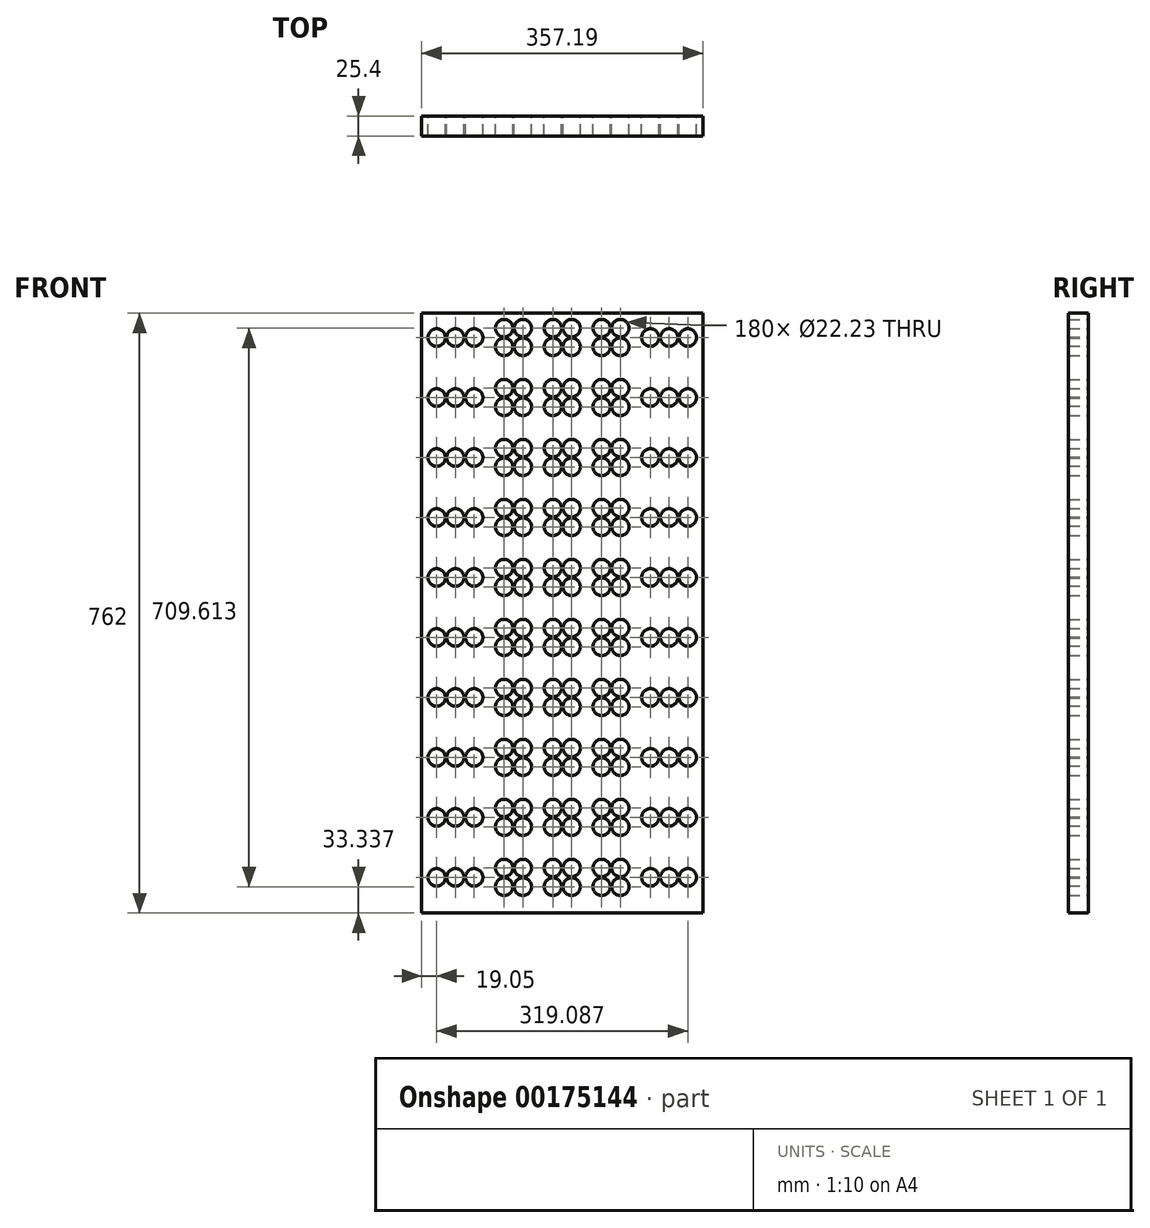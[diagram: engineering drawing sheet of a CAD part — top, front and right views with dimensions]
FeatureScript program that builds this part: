
annotation { "Feature Type Name" : "Feature", "Feature Type Description" : "" }
export const myFeature = defineFeature(function(context is Context, id is Id, definition is map)
    precondition{}
    {
        {
            var Q0;
            Q0=qCreatedBy(makeId("Front.planeOp"),FACE);
            var sketch = newSketch(context, id + "F0", { "sketchPlane" : qUnion([Q0])});
            skLineSegment(sketch, "E0", {"start": v(0, 0) * mm, "end": v(0, 762) * mm});
            skLineSegment(sketch, "E1", {"start": v(0, 762) * mm, "end": v(357.19, 762) * mm});
            skLineSegment(sketch, "E2", {"start": v(357.19, 762) * mm, "end": v(357.19, 0) * mm});
            skLineSegment(sketch, "E3", {"start": v(357.19, 0) * mm, "end": v(0, 0) * mm});
            skCircle(sketch, "E4", {"center": v(137.16, 742.95) * mm, "radius": 11.11 * mm});
            skCircle(sketch, "E5", {"center": v(137.16, 719.14) * mm, "radius": 11.11 * mm});
            skCircle(sketch, "E6", {"center": v(160.97, 742.95) * mm, "radius": 11.11 * mm});
            skCircle(sketch, "E7", {"center": v(160.97, 719.14) * mm, "radius": 11.11 * mm});
            skLineSegment(sketch, "E8", {"start": v(137.16, 742.95) * mm, "end": v(160.97, 742.95) * mm, "construction": true});
            skLineSegment(sketch, "E9", {"start": v(160.97, 719.14) * mm, "end": v(160.97, 742.95) * mm, "construction": true});
            skLineSegment(sketch, "E10", {"start": v(137.16, 742.95) * mm, "end": v(137.16, 719.14) * mm, "construction": true});
            skLineSegment(sketch, "E11", {"start": v(137.16, 719.14) * mm, "end": v(160.97, 719.14) * mm, "construction": true});
            skCircle(sketch, "E12", {"center": v(196.22, 742.95) * mm, "radius": 11.11 * mm});
            skCircle(sketch, "E13", {"center": v(220.03, 742.95) * mm, "radius": 11.11 * mm});
            skCircle(sketch, "E14", {"center": v(220.03, 719.14) * mm, "radius": 11.11 * mm});
            skCircle(sketch, "E15", {"center": v(196.22, 719.14) * mm, "radius": 11.11 * mm});
            skCircle(sketch, "E16", {"center": v(255.27, 742.95) * mm, "radius": 11.11 * mm});
            skCircle(sketch, "E17", {"center": v(279.08, 742.95) * mm, "radius": 11.11 * mm});
            skCircle(sketch, "E18", {"center": v(255.27, 719.14) * mm, "radius": 11.11 * mm});
            skCircle(sketch, "E19", {"center": v(279.08, 719.14) * mm, "radius": 11.11 * mm});
            skCircle(sketch, "E20", {"center": v(314.33, 742.95) * mm, "radius": 11.11 * mm});
            skCircle(sketch, "E21", {"center": v(314.33, 719.14) * mm, "radius": 11.11 * mm});
            skCircle(sketch, "E22", {"center": v(338.14, 719.14) * mm, "radius": 11.11 * mm});
            skCircle(sketch, "E23", {"center": v(338.14, 742.95) * mm, "radius": 11.11 * mm});
            skLineSegment(sketch, "E24", {"start": v(196.22, 742.95) * mm, "end": v(220.03, 742.95) * mm, "construction": true});
            skLineSegment(sketch, "E25", {"start": v(220.03, 742.95) * mm, "end": v(220.03, 719.14) * mm, "construction": true});
            skLineSegment(sketch, "E26", {"start": v(220.03, 719.14) * mm, "end": v(196.22, 719.14) * mm, "construction": true});
            skLineSegment(sketch, "E27", {"start": v(196.22, 719.14) * mm, "end": v(196.22, 742.95) * mm, "construction": true});
            skLineSegment(sketch, "E28", {"start": v(255.27, 742.95) * mm, "end": v(279.08, 742.95) * mm, "construction": true});
            skLineSegment(sketch, "E29", {"start": v(279.08, 742.95) * mm, "end": v(279.08, 719.14) * mm, "construction": true});
            skLineSegment(sketch, "E30", {"start": v(279.08, 719.14) * mm, "end": v(255.27, 719.14) * mm, "construction": true});
            skLineSegment(sketch, "E31", {"start": v(255.27, 719.14) * mm, "end": v(255.27, 742.95) * mm, "construction": true});
            skLineSegment(sketch, "E32", {"start": v(314.33, 742.95) * mm, "end": v(338.14, 742.95) * mm, "construction": true});
            skLineSegment(sketch, "E33", {"start": v(338.14, 719.14) * mm, "end": v(314.33, 719.14) * mm, "construction": true});
            skLineSegment(sketch, "E34", {"start": v(314.33, 719.14) * mm, "end": v(314.33, 742.95) * mm, "construction": true});
            skLineSegment(sketch, "E35", {"start": v(338.14, 742.95) * mm, "end": v(338.14, 719.14) * mm, "construction": true});
            skLineSegment(sketch, "E36", {"start": v(220.03, 731.04) * mm, "end": v(255.27, 731.04) * mm, "construction": true});
            skLineSegment(sketch, "E37", {"start": v(279.08, 731.04) * mm, "end": v(314.33, 731.04) * mm, "construction": true});
            skLineSegment(sketch, "E38", {"start": v(196.22, 731.04) * mm, "end": v(160.97, 731.04) * mm, "construction": true});
            skCircle(sketch, "E39", {"center": v(19.05, 719.14) * mm, "radius": 11.11 * mm});
            skCircle(sketch, "E40", {"center": v(42.86, 742.95) * mm, "radius": 11.11 * mm});
            skCircle(sketch, "E41", {"center": v(42.86, 719.14) * mm, "radius": 11.11 * mm});
            skCircle(sketch, "E42", {"center": v(19.05, 742.95) * mm, "radius": 11.11 * mm});
            skCircle(sketch, "E43", {"center": v(78.1, 742.95) * mm, "radius": 11.11 * mm});
            skCircle(sketch, "E44", {"center": v(101.92, 742.95) * mm, "radius": 11.11 * mm});
            skCircle(sketch, "E45", {"center": v(101.92, 719.14) * mm, "radius": 11.11 * mm});
            skCircle(sketch, "E46", {"center": v(78.1, 719.14) * mm, "radius": 11.11 * mm});
            skLineSegment(sketch, "E47", {"start": v(19.05, 742.95) * mm, "end": v(42.86, 742.95) * mm, "construction": true});
            skLineSegment(sketch, "E48", {"start": v(42.86, 742.95) * mm, "end": v(42.86, 719.14) * mm, "construction": true});
            skLineSegment(sketch, "E49", {"start": v(19.05, 719.14) * mm, "end": v(42.86, 719.14) * mm, "construction": true});
            skLineSegment(sketch, "E50", {"start": v(19.05, 719.14) * mm, "end": v(19.05, 742.95) * mm, "construction": true});
            skLineSegment(sketch, "E51", {"start": v(78.1, 742.95) * mm, "end": v(101.92, 742.95) * mm, "construction": true});
            skLineSegment(sketch, "E52", {"start": v(101.92, 742.95) * mm, "end": v(101.92, 719.14) * mm, "construction": true});
            skLineSegment(sketch, "E53", {"start": v(101.92, 719.14) * mm, "end": v(78.1, 719.14) * mm, "construction": true});
            skLineSegment(sketch, "E54", {"start": v(78.1, 719.14) * mm, "end": v(78.1, 742.95) * mm, "construction": true});
            skLineSegment(sketch, "E55", {"start": v(42.86, 731.04) * mm, "end": v(78.1, 731.04) * mm, "construction": true});
            skLineSegment(sketch, "E56", {"start": v(19.05, 731.04) * mm, "end": v(0, 731.04) * mm, "construction": true});
            skLineSegment(sketch, "E57", {"start": v(338.14, 731.04) * mm, "end": v(357.19, 731.04) * mm, "construction": true});
            skLineSegment(sketch, "E58", {"start": v(101.92, 731.04) * mm, "end": v(137.16, 731.04) * mm, "construction": true});
            skLineSegment(sketch, "E59", {"start": v(326.23, 742.95) * mm, "end": v(326.23, 762) * mm, "construction": true});
            skLineSegment(sketch, "E60", {"start": v(113.03, 742.95) * mm, "end": v(113.03, 719.14) * mm, "construction": true});
            skLineSegment(sketch, "E61", {"start": v(126.05, 742.95) * mm, "end": v(126.05, 719.14) * mm, "construction": true});
            skSolve(sketch);
        }
        {
            var Q0;
            Q0=qCreatedBy(makeId("Front.planeOp"),FACE);
            var sketch = newSketch(context, id + "F1", { "sketchPlane" : qUnion([Q0])});
            skLineSegment(sketch, "E62", {"start": v(0, 0) * mm, "end": v(0, 762) * mm});
            skLineSegment(sketch, "E63", {"start": v(0, 762) * mm, "end": v(357.19, 762) * mm});
            skLineSegment(sketch, "E64", {"start": v(357.19, 762) * mm, "end": v(357.19, 0) * mm});
            skLineSegment(sketch, "E65", {"start": v(357.19, 0) * mm, "end": v(0, 0) * mm});
            skCircle(sketch, "E66", {"center": v(166.69, 742.95) * mm, "radius": 11.11 * mm});
            skCircle(sketch, "E67", {"center": v(166.69, 719.14) * mm, "radius": 11.11 * mm});
            skCircle(sketch, "E68", {"center": v(190.5, 742.95) * mm, "radius": 11.11 * mm});
            skCircle(sketch, "E69", {"center": v(190.5, 719.14) * mm, "radius": 11.11 * mm});
            skLineSegment(sketch, "E70", {"start": v(166.69, 742.95) * mm, "end": v(190.5, 742.95) * mm, "construction": true});
            skLineSegment(sketch, "E71", {"start": v(190.5, 719.14) * mm, "end": v(190.5, 742.95) * mm, "construction": true});
            skLineSegment(sketch, "E72", {"start": v(166.69, 742.95) * mm, "end": v(166.69, 719.14) * mm, "construction": true});
            skLineSegment(sketch, "E73", {"start": v(166.69, 719.14) * mm, "end": v(190.5, 719.14) * mm, "construction": true});
            skCircle(sketch, "E74", {"center": v(252.41, 742.95) * mm, "radius": 11.11 * mm});
            skCircle(sketch, "E75", {"center": v(228.6, 742.95) * mm, "radius": 11.11 * mm});
            skCircle(sketch, "E76", {"center": v(252.41, 719.14) * mm, "radius": 11.11 * mm});
            skCircle(sketch, "E77", {"center": v(228.6, 719.14) * mm, "radius": 11.11 * mm});
            skCircle(sketch, "E78", {"center": v(314.33, 731.04) * mm, "radius": 11.11 * mm});
            skCircle(sketch, "E79", {"center": v(338.14, 731.04) * mm, "radius": 11.11 * mm});
            skLineSegment(sketch, "E80", {"start": v(228.6, 742.95) * mm, "end": v(252.41, 742.95) * mm, "construction": true});
            skLineSegment(sketch, "E81", {"start": v(228.6, 742.95) * mm, "end": v(228.6, 719.14) * mm, "construction": true});
            skLineSegment(sketch, "E82", {"start": v(252.41, 719.14) * mm, "end": v(228.6, 719.14) * mm, "construction": true});
            skLineSegment(sketch, "E83", {"start": v(252.41, 719.14) * mm, "end": v(252.41, 742.95) * mm, "construction": true});
            skLineSegment(sketch, "E84", {"start": v(338.14, 731.04) * mm, "end": v(314.33, 731.04) * mm, "construction": true});
            skCircle(sketch, "E85", {"center": v(104.78, 719.14) * mm, "radius": 11.11 * mm});
            skCircle(sketch, "E86", {"center": v(128.59, 719.14) * mm, "radius": 11.11 * mm});
            skCircle(sketch, "E87", {"center": v(128.59, 742.95) * mm, "radius": 11.11 * mm});
            skCircle(sketch, "E88", {"center": v(104.78, 742.95) * mm, "radius": 11.11 * mm});
            skLineSegment(sketch, "E89", {"start": v(104.78, 719.14) * mm, "end": v(128.59, 719.14) * mm, "construction": true});
            skLineSegment(sketch, "E90", {"start": v(128.59, 742.95) * mm, "end": v(128.59, 719.14) * mm, "construction": true});
            skLineSegment(sketch, "E91", {"start": v(128.59, 742.95) * mm, "end": v(104.78, 742.95) * mm, "construction": true});
            skLineSegment(sketch, "E92", {"start": v(104.78, 719.14) * mm, "end": v(104.78, 742.95) * mm, "construction": true});
            skLineSegment(sketch, "E93", {"start": v(19.05, 731.04) * mm, "end": v(0, 731.04) * mm, "construction": true});
            skLineSegment(sketch, "E94", {"start": v(338.14, 731.04) * mm, "end": v(357.19, 731.04) * mm, "construction": true});
            skLineSegment(sketch, "E95", {"start": v(139.7, 742.95) * mm, "end": v(139.7, 719.14) * mm, "construction": true});
            skLineSegment(sketch, "E96", {"start": v(155.57, 742.95) * mm, "end": v(155.57, 719.14) * mm, "construction": true});
            skCircle(sketch, "E97", {"center": v(290.51, 731.04) * mm, "radius": 11.11 * mm});
            skCircle(sketch, "E98", {"center": v(19.05, 731.04) * mm, "radius": 11.11 * mm});
            skCircle(sketch, "E99", {"center": v(42.86, 731.04) * mm, "radius": 11.11 * mm});
            skCircle(sketch, "E100", {"center": v(66.68, 731.04) * mm, "radius": 11.11 * mm});
            skLineSegment(sketch, "E101", {"start": v(19.05, 731.04) * mm, "end": v(42.86, 731.04) * mm, "construction": true});
            skLineSegment(sketch, "E102", {"start": v(42.86, 731.04) * mm, "end": v(66.68, 731.04) * mm, "construction": true});
            skLineSegment(sketch, "E103", {"start": v(290.51, 731.04) * mm, "end": v(314.33, 731.04) * mm, "construction": true});
            skLineSegment(sketch, "E104", {"start": v(252.41, 731.04) * mm, "end": v(290.51, 731.04) * mm, "construction": true});
            skLineSegment(sketch, "E105", {"start": v(228.6, 731.04) * mm, "end": v(190.5, 731.04) * mm, "construction": true});
            skLineSegment(sketch, "E106", {"start": v(128.59, 731.04) * mm, "end": v(166.69, 731.04) * mm, "construction": true});
            skLineSegment(sketch, "E107", {"start": v(104.78, 731.04) * mm, "end": v(66.68, 731.04) * mm, "construction": true});
            skLineSegment(sketch, "E108", {"start": v(240.5, 742.95) * mm, "end": v(240.5, 762) * mm, "construction": true});
            skCircle(sketch, "E109.0.1.0", {"center": v(66.67, 654.84) * mm, "radius": 11.11 * mm});
            skLineSegment(sketch, "E109.0.1.1", {"start": v(19.05, 654.84) * mm, "end": v(42.86, 654.84) * mm, "construction": true});
            skCircle(sketch, "E109.0.1.2", {"center": v(252.41, 642.94) * mm, "radius": 11.11 * mm});
            skLineSegment(sketch, "E109.0.1.3", {"start": v(104.78, 642.94) * mm, "end": v(128.59, 642.94) * mm, "construction": true});
            skLineSegment(sketch, "E109.0.1.4", {"start": v(19.05, 654.84) * mm, "end": v(0, 654.84) * mm, "construction": true});
            skCircle(sketch, "E109.0.1.5", {"center": v(228.6, 642.94) * mm, "radius": 11.11 * mm});
            skLineSegment(sketch, "E109.0.1.6", {"start": v(252.41, 642.94) * mm, "end": v(228.6, 642.94) * mm, "construction": true});
            skCircle(sketch, "E109.0.1.7", {"center": v(19.05, 654.84) * mm, "radius": 11.11 * mm});
            skCircle(sketch, "E109.0.1.8", {"center": v(128.59, 642.94) * mm, "radius": 11.11 * mm});
            skCircle(sketch, "E109.0.1.9", {"center": v(314.33, 654.84) * mm, "radius": 11.11 * mm});
            skCircle(sketch, "E109.0.1.10", {"center": v(338.14, 654.84) * mm, "radius": 11.11 * mm});
            skCircle(sketch, "E109.0.1.11", {"center": v(166.69, 642.94) * mm, "radius": 11.11 * mm});
            skCircle(sketch, "E109.0.1.12", {"center": v(190.5, 642.94) * mm, "radius": 11.11 * mm});
            skCircle(sketch, "E109.0.1.13", {"center": v(104.78, 642.94) * mm, "radius": 11.11 * mm});
            skCircle(sketch, "E109.0.1.14", {"center": v(42.86, 654.84) * mm, "radius": 11.11 * mm});
            skCircle(sketch, "E109.0.1.15", {"center": v(290.51, 654.84) * mm, "radius": 11.11 * mm});
            skLineSegment(sketch, "E109.0.1.16", {"start": v(290.51, 654.84) * mm, "end": v(314.33, 654.84) * mm, "construction": true});
            skCircle(sketch, "E109.0.1.17", {"center": v(128.59, 666.75) * mm, "radius": 11.11 * mm});
            skLineSegment(sketch, "E109.0.1.18", {"start": v(338.14, 654.84) * mm, "end": v(314.33, 654.84) * mm, "construction": true});
            skLineSegment(sketch, "E109.0.1.19", {"start": v(42.86, 654.84) * mm, "end": v(66.67, 654.84) * mm, "construction": true});
            skLineSegment(sketch, "E109.0.1.20", {"start": v(128.59, 666.75) * mm, "end": v(104.78, 666.75) * mm, "construction": true});
            skLineSegment(sketch, "E109.0.1.21", {"start": v(228.6, 654.84) * mm, "end": v(190.5, 654.84) * mm, "construction": true});
            skLineSegment(sketch, "E109.0.1.22", {"start": v(338.14, 654.84) * mm, "end": v(357.19, 654.84) * mm, "construction": true});
            skCircle(sketch, "E109.0.1.23", {"center": v(228.6, 666.75) * mm, "radius": 11.11 * mm});
            skCircle(sketch, "E109.0.1.24", {"center": v(104.78, 666.75) * mm, "radius": 11.11 * mm});
            skLineSegment(sketch, "E109.0.1.25", {"start": v(104.78, 654.84) * mm, "end": v(66.67, 654.84) * mm, "construction": true});
            skCircle(sketch, "E109.0.1.26", {"center": v(166.69, 666.75) * mm, "radius": 11.11 * mm});
            skCircle(sketch, "E109.0.1.27", {"center": v(252.41, 666.75) * mm, "radius": 11.11 * mm});
            skLineSegment(sketch, "E109.0.1.28", {"start": v(166.69, 666.75) * mm, "end": v(190.5, 666.75) * mm, "construction": true});
            skLineSegment(sketch, "E109.0.1.29", {"start": v(166.69, 642.94) * mm, "end": v(190.5, 642.94) * mm, "construction": true});
            skCircle(sketch, "E109.0.1.30", {"center": v(190.5, 666.75) * mm, "radius": 11.11 * mm});
            skLineSegment(sketch, "E109.0.1.31", {"start": v(252.41, 654.84) * mm, "end": v(290.51, 654.84) * mm, "construction": true});
            skLineSegment(sketch, "E109.0.1.32", {"start": v(252.41, 642.94) * mm, "end": v(252.41, 666.75) * mm, "construction": true});
            skLineSegment(sketch, "E109.0.1.33", {"start": v(104.78, 642.94) * mm, "end": v(104.78, 666.75) * mm, "construction": true});
            skLineSegment(sketch, "E109.0.1.34", {"start": v(155.58, 666.75) * mm, "end": v(155.58, 642.94) * mm, "construction": true});
            skLineSegment(sketch, "E109.0.1.35", {"start": v(228.6, 666.75) * mm, "end": v(252.41, 666.75) * mm, "construction": true});
            skLineSegment(sketch, "E109.0.1.36", {"start": v(139.7, 666.75) * mm, "end": v(139.7, 642.94) * mm, "construction": true});
            skLineSegment(sketch, "E109.0.1.37", {"start": v(128.59, 654.84) * mm, "end": v(166.69, 654.84) * mm, "construction": true});
            skLineSegment(sketch, "E109.0.1.38", {"start": v(228.6, 666.75) * mm, "end": v(228.6, 642.94) * mm, "construction": true});
            skLineSegment(sketch, "E109.0.1.39", {"start": v(166.69, 666.75) * mm, "end": v(166.69, 642.94) * mm, "construction": true});
            skLineSegment(sketch, "E109.0.1.40", {"start": v(190.5, 642.94) * mm, "end": v(190.5, 666.75) * mm, "construction": true});
            skLineSegment(sketch, "E109.0.1.41", {"start": v(128.59, 666.75) * mm, "end": v(128.59, 642.94) * mm, "construction": true});
            skCircle(sketch, "E109.0.2.0", {"center": v(66.67, 578.64) * mm, "radius": 11.11 * mm});
            skLineSegment(sketch, "E109.0.2.1", {"start": v(19.05, 578.64) * mm, "end": v(42.86, 578.64) * mm, "construction": true});
            skCircle(sketch, "E109.0.2.2", {"center": v(252.41, 566.74) * mm, "radius": 11.11 * mm});
            skLineSegment(sketch, "E109.0.2.3", {"start": v(104.78, 566.74) * mm, "end": v(128.59, 566.74) * mm, "construction": true});
            skLineSegment(sketch, "E109.0.2.4", {"start": v(19.05, 578.64) * mm, "end": v(0, 578.64) * mm, "construction": true});
            skCircle(sketch, "E109.0.2.5", {"center": v(228.6, 566.74) * mm, "radius": 11.11 * mm});
            skLineSegment(sketch, "E109.0.2.6", {"start": v(252.41, 566.74) * mm, "end": v(228.6, 566.74) * mm, "construction": true});
            skCircle(sketch, "E109.0.2.7", {"center": v(19.05, 578.64) * mm, "radius": 11.11 * mm});
            skCircle(sketch, "E109.0.2.8", {"center": v(128.59, 566.74) * mm, "radius": 11.11 * mm});
            skCircle(sketch, "E109.0.2.9", {"center": v(314.33, 578.64) * mm, "radius": 11.11 * mm});
            skCircle(sketch, "E109.0.2.10", {"center": v(338.14, 578.64) * mm, "radius": 11.11 * mm});
            skCircle(sketch, "E109.0.2.11", {"center": v(166.69, 566.74) * mm, "radius": 11.11 * mm});
            skCircle(sketch, "E109.0.2.12", {"center": v(190.5, 566.74) * mm, "radius": 11.11 * mm});
            skCircle(sketch, "E109.0.2.13", {"center": v(104.78, 566.74) * mm, "radius": 11.11 * mm});
            skCircle(sketch, "E109.0.2.14", {"center": v(42.86, 578.64) * mm, "radius": 11.11 * mm});
            skCircle(sketch, "E109.0.2.15", {"center": v(290.51, 578.64) * mm, "radius": 11.11 * mm});
            skLineSegment(sketch, "E109.0.2.16", {"start": v(290.51, 578.64) * mm, "end": v(314.33, 578.64) * mm, "construction": true});
            skCircle(sketch, "E109.0.2.17", {"center": v(128.59, 590.55) * mm, "radius": 11.11 * mm});
            skLineSegment(sketch, "E109.0.2.18", {"start": v(338.14, 578.64) * mm, "end": v(314.33, 578.64) * mm, "construction": true});
            skLineSegment(sketch, "E109.0.2.19", {"start": v(42.86, 578.64) * mm, "end": v(66.67, 578.64) * mm, "construction": true});
            skLineSegment(sketch, "E109.0.2.20", {"start": v(128.59, 590.55) * mm, "end": v(104.78, 590.55) * mm, "construction": true});
            skLineSegment(sketch, "E109.0.2.21", {"start": v(228.6, 578.64) * mm, "end": v(190.5, 578.64) * mm, "construction": true});
            skLineSegment(sketch, "E109.0.2.22", {"start": v(338.14, 578.64) * mm, "end": v(357.19, 578.64) * mm, "construction": true});
            skCircle(sketch, "E109.0.2.23", {"center": v(228.6, 590.55) * mm, "radius": 11.11 * mm});
            skCircle(sketch, "E109.0.2.24", {"center": v(104.78, 590.55) * mm, "radius": 11.11 * mm});
            skLineSegment(sketch, "E109.0.2.25", {"start": v(104.78, 578.64) * mm, "end": v(66.67, 578.64) * mm, "construction": true});
            skCircle(sketch, "E109.0.2.26", {"center": v(166.69, 590.55) * mm, "radius": 11.11 * mm});
            skCircle(sketch, "E109.0.2.27", {"center": v(252.41, 590.55) * mm, "radius": 11.11 * mm});
            skLineSegment(sketch, "E109.0.2.28", {"start": v(166.69, 590.55) * mm, "end": v(190.5, 590.55) * mm, "construction": true});
            skLineSegment(sketch, "E109.0.2.29", {"start": v(166.69, 566.74) * mm, "end": v(190.5, 566.74) * mm, "construction": true});
            skCircle(sketch, "E109.0.2.30", {"center": v(190.5, 590.55) * mm, "radius": 11.11 * mm});
            skLineSegment(sketch, "E109.0.2.31", {"start": v(252.41, 578.64) * mm, "end": v(290.51, 578.64) * mm, "construction": true});
            skLineSegment(sketch, "E109.0.2.32", {"start": v(252.41, 566.74) * mm, "end": v(252.41, 590.55) * mm, "construction": true});
            skLineSegment(sketch, "E109.0.2.33", {"start": v(104.78, 566.74) * mm, "end": v(104.78, 590.55) * mm, "construction": true});
            skLineSegment(sketch, "E109.0.2.34", {"start": v(155.58, 590.55) * mm, "end": v(155.58, 566.74) * mm, "construction": true});
            skLineSegment(sketch, "E109.0.2.35", {"start": v(228.6, 590.55) * mm, "end": v(252.41, 590.55) * mm, "construction": true});
            skLineSegment(sketch, "E109.0.2.36", {"start": v(139.7, 590.55) * mm, "end": v(139.7, 566.74) * mm, "construction": true});
            skLineSegment(sketch, "E109.0.2.37", {"start": v(128.59, 578.64) * mm, "end": v(166.69, 578.64) * mm, "construction": true});
            skLineSegment(sketch, "E109.0.2.38", {"start": v(228.6, 590.55) * mm, "end": v(228.6, 566.74) * mm, "construction": true});
            skLineSegment(sketch, "E109.0.2.39", {"start": v(166.69, 590.55) * mm, "end": v(166.69, 566.74) * mm, "construction": true});
            skLineSegment(sketch, "E109.0.2.40", {"start": v(190.5, 566.74) * mm, "end": v(190.5, 590.55) * mm, "construction": true});
            skLineSegment(sketch, "E109.0.2.41", {"start": v(128.59, 590.55) * mm, "end": v(128.59, 566.74) * mm, "construction": true});
            skCircle(sketch, "E109.0.3.0", {"center": v(66.67, 502.44) * mm, "radius": 11.11 * mm});
            skLineSegment(sketch, "E109.0.3.1", {"start": v(19.05, 502.44) * mm, "end": v(42.86, 502.44) * mm, "construction": true});
            skCircle(sketch, "E109.0.3.2", {"center": v(252.41, 490.54) * mm, "radius": 11.11 * mm});
            skLineSegment(sketch, "E109.0.3.3", {"start": v(104.78, 490.54) * mm, "end": v(128.59, 490.54) * mm, "construction": true});
            skLineSegment(sketch, "E109.0.3.4", {"start": v(19.05, 502.44) * mm, "end": v(0, 502.44) * mm, "construction": true});
            skCircle(sketch, "E109.0.3.5", {"center": v(228.6, 490.54) * mm, "radius": 11.11 * mm});
            skLineSegment(sketch, "E109.0.3.6", {"start": v(252.41, 490.54) * mm, "end": v(228.6, 490.54) * mm, "construction": true});
            skCircle(sketch, "E109.0.3.7", {"center": v(19.05, 502.44) * mm, "radius": 11.11 * mm});
            skCircle(sketch, "E109.0.3.8", {"center": v(128.59, 490.54) * mm, "radius": 11.11 * mm});
            skCircle(sketch, "E109.0.3.9", {"center": v(314.33, 502.44) * mm, "radius": 11.11 * mm});
            skCircle(sketch, "E109.0.3.10", {"center": v(338.14, 502.44) * mm, "radius": 11.11 * mm});
            skCircle(sketch, "E109.0.3.11", {"center": v(166.69, 490.54) * mm, "radius": 11.11 * mm});
            skCircle(sketch, "E109.0.3.12", {"center": v(190.5, 490.54) * mm, "radius": 11.11 * mm});
            skCircle(sketch, "E109.0.3.13", {"center": v(104.78, 490.54) * mm, "radius": 11.11 * mm});
            skCircle(sketch, "E109.0.3.14", {"center": v(42.86, 502.44) * mm, "radius": 11.11 * mm});
            skCircle(sketch, "E109.0.3.15", {"center": v(290.51, 502.44) * mm, "radius": 11.11 * mm});
            skLineSegment(sketch, "E109.0.3.16", {"start": v(290.51, 502.44) * mm, "end": v(314.33, 502.44) * mm, "construction": true});
            skCircle(sketch, "E109.0.3.17", {"center": v(128.59, 514.35) * mm, "radius": 11.11 * mm});
            skLineSegment(sketch, "E109.0.3.18", {"start": v(338.14, 502.44) * mm, "end": v(314.33, 502.44) * mm, "construction": true});
            skLineSegment(sketch, "E109.0.3.19", {"start": v(42.86, 502.44) * mm, "end": v(66.67, 502.44) * mm, "construction": true});
            skLineSegment(sketch, "E109.0.3.20", {"start": v(128.59, 514.35) * mm, "end": v(104.78, 514.35) * mm, "construction": true});
            skLineSegment(sketch, "E109.0.3.21", {"start": v(228.6, 502.44) * mm, "end": v(190.5, 502.44) * mm, "construction": true});
            skLineSegment(sketch, "E109.0.3.22", {"start": v(338.14, 502.44) * mm, "end": v(357.19, 502.44) * mm, "construction": true});
            skCircle(sketch, "E109.0.3.23", {"center": v(228.6, 514.35) * mm, "radius": 11.11 * mm});
            skCircle(sketch, "E109.0.3.24", {"center": v(104.78, 514.35) * mm, "radius": 11.11 * mm});
            skLineSegment(sketch, "E109.0.3.25", {"start": v(104.78, 502.44) * mm, "end": v(66.67, 502.44) * mm, "construction": true});
            skCircle(sketch, "E109.0.3.26", {"center": v(166.69, 514.35) * mm, "radius": 11.11 * mm});
            skCircle(sketch, "E109.0.3.27", {"center": v(252.41, 514.35) * mm, "radius": 11.11 * mm});
            skLineSegment(sketch, "E109.0.3.28", {"start": v(166.69, 514.35) * mm, "end": v(190.5, 514.35) * mm, "construction": true});
            skLineSegment(sketch, "E109.0.3.29", {"start": v(166.69, 490.54) * mm, "end": v(190.5, 490.54) * mm, "construction": true});
            skCircle(sketch, "E109.0.3.30", {"center": v(190.5, 514.35) * mm, "radius": 11.11 * mm});
            skLineSegment(sketch, "E109.0.3.31", {"start": v(252.41, 502.44) * mm, "end": v(290.51, 502.44) * mm, "construction": true});
            skLineSegment(sketch, "E109.0.3.32", {"start": v(252.41, 490.54) * mm, "end": v(252.41, 514.35) * mm, "construction": true});
            skLineSegment(sketch, "E109.0.3.33", {"start": v(104.78, 490.54) * mm, "end": v(104.78, 514.35) * mm, "construction": true});
            skLineSegment(sketch, "E109.0.3.34", {"start": v(155.58, 514.35) * mm, "end": v(155.58, 490.54) * mm, "construction": true});
            skLineSegment(sketch, "E109.0.3.35", {"start": v(228.6, 514.35) * mm, "end": v(252.41, 514.35) * mm, "construction": true});
            skLineSegment(sketch, "E109.0.3.36", {"start": v(139.7, 514.35) * mm, "end": v(139.7, 490.54) * mm, "construction": true});
            skLineSegment(sketch, "E109.0.3.37", {"start": v(128.59, 502.44) * mm, "end": v(166.69, 502.44) * mm, "construction": true});
            skLineSegment(sketch, "E109.0.3.38", {"start": v(228.6, 514.35) * mm, "end": v(228.6, 490.54) * mm, "construction": true});
            skLineSegment(sketch, "E109.0.3.39", {"start": v(166.69, 514.35) * mm, "end": v(166.69, 490.54) * mm, "construction": true});
            skLineSegment(sketch, "E109.0.3.40", {"start": v(190.5, 490.54) * mm, "end": v(190.5, 514.35) * mm, "construction": true});
            skLineSegment(sketch, "E109.0.3.41", {"start": v(128.59, 514.35) * mm, "end": v(128.59, 490.54) * mm, "construction": true});
            skCircle(sketch, "E109.0.4.0", {"center": v(66.67, 426.24) * mm, "radius": 11.11 * mm});
            skLineSegment(sketch, "E109.0.4.1", {"start": v(19.05, 426.24) * mm, "end": v(42.86, 426.24) * mm, "construction": true});
            skCircle(sketch, "E109.0.4.2", {"center": v(252.41, 414.34) * mm, "radius": 11.11 * mm});
            skLineSegment(sketch, "E109.0.4.3", {"start": v(104.78, 414.34) * mm, "end": v(128.59, 414.34) * mm, "construction": true});
            skLineSegment(sketch, "E109.0.4.4", {"start": v(19.05, 426.24) * mm, "end": v(0, 426.24) * mm, "construction": true});
            skCircle(sketch, "E109.0.4.5", {"center": v(228.6, 414.34) * mm, "radius": 11.11 * mm});
            skLineSegment(sketch, "E109.0.4.6", {"start": v(252.41, 414.34) * mm, "end": v(228.6, 414.34) * mm, "construction": true});
            skCircle(sketch, "E109.0.4.7", {"center": v(19.05, 426.24) * mm, "radius": 11.11 * mm});
            skCircle(sketch, "E109.0.4.8", {"center": v(128.59, 414.34) * mm, "radius": 11.11 * mm});
            skCircle(sketch, "E109.0.4.9", {"center": v(314.33, 426.24) * mm, "radius": 11.11 * mm});
            skCircle(sketch, "E109.0.4.10", {"center": v(338.14, 426.24) * mm, "radius": 11.11 * mm});
            skCircle(sketch, "E109.0.4.11", {"center": v(166.69, 414.34) * mm, "radius": 11.11 * mm});
            skCircle(sketch, "E109.0.4.12", {"center": v(190.5, 414.34) * mm, "radius": 11.11 * mm});
            skCircle(sketch, "E109.0.4.13", {"center": v(104.78, 414.34) * mm, "radius": 11.11 * mm});
            skCircle(sketch, "E109.0.4.14", {"center": v(42.86, 426.24) * mm, "radius": 11.11 * mm});
            skCircle(sketch, "E109.0.4.15", {"center": v(290.51, 426.24) * mm, "radius": 11.11 * mm});
            skLineSegment(sketch, "E109.0.4.16", {"start": v(290.51, 426.24) * mm, "end": v(314.33, 426.24) * mm, "construction": true});
            skCircle(sketch, "E109.0.4.17", {"center": v(128.59, 438.15) * mm, "radius": 11.11 * mm});
            skLineSegment(sketch, "E109.0.4.18", {"start": v(338.14, 426.24) * mm, "end": v(314.33, 426.24) * mm, "construction": true});
            skLineSegment(sketch, "E109.0.4.19", {"start": v(42.86, 426.24) * mm, "end": v(66.67, 426.24) * mm, "construction": true});
            skLineSegment(sketch, "E109.0.4.20", {"start": v(128.59, 438.15) * mm, "end": v(104.78, 438.15) * mm, "construction": true});
            skLineSegment(sketch, "E109.0.4.21", {"start": v(228.6, 426.24) * mm, "end": v(190.5, 426.24) * mm, "construction": true});
            skLineSegment(sketch, "E109.0.4.22", {"start": v(338.14, 426.24) * mm, "end": v(357.19, 426.24) * mm, "construction": true});
            skCircle(sketch, "E109.0.4.23", {"center": v(228.6, 438.15) * mm, "radius": 11.11 * mm});
            skCircle(sketch, "E109.0.4.24", {"center": v(104.78, 438.15) * mm, "radius": 11.11 * mm});
            skLineSegment(sketch, "E109.0.4.25", {"start": v(104.78, 426.24) * mm, "end": v(66.67, 426.24) * mm, "construction": true});
            skCircle(sketch, "E109.0.4.26", {"center": v(166.69, 438.15) * mm, "radius": 11.11 * mm});
            skCircle(sketch, "E109.0.4.27", {"center": v(252.41, 438.15) * mm, "radius": 11.11 * mm});
            skLineSegment(sketch, "E109.0.4.28", {"start": v(166.69, 438.15) * mm, "end": v(190.5, 438.15) * mm, "construction": true});
            skLineSegment(sketch, "E109.0.4.29", {"start": v(166.69, 414.34) * mm, "end": v(190.5, 414.34) * mm, "construction": true});
            skCircle(sketch, "E109.0.4.30", {"center": v(190.5, 438.15) * mm, "radius": 11.11 * mm});
            skLineSegment(sketch, "E109.0.4.31", {"start": v(252.41, 426.24) * mm, "end": v(290.51, 426.24) * mm, "construction": true});
            skLineSegment(sketch, "E109.0.4.32", {"start": v(252.41, 414.34) * mm, "end": v(252.41, 438.15) * mm, "construction": true});
            skLineSegment(sketch, "E109.0.4.33", {"start": v(104.78, 414.34) * mm, "end": v(104.78, 438.15) * mm, "construction": true});
            skLineSegment(sketch, "E109.0.4.34", {"start": v(155.58, 438.15) * mm, "end": v(155.58, 414.34) * mm, "construction": true});
            skLineSegment(sketch, "E109.0.4.35", {"start": v(228.6, 438.15) * mm, "end": v(252.41, 438.15) * mm, "construction": true});
            skLineSegment(sketch, "E109.0.4.36", {"start": v(139.7, 438.15) * mm, "end": v(139.7, 414.34) * mm, "construction": true});
            skLineSegment(sketch, "E109.0.4.37", {"start": v(128.59, 426.24) * mm, "end": v(166.69, 426.24) * mm, "construction": true});
            skLineSegment(sketch, "E109.0.4.38", {"start": v(228.6, 438.15) * mm, "end": v(228.6, 414.34) * mm, "construction": true});
            skLineSegment(sketch, "E109.0.4.39", {"start": v(166.69, 438.15) * mm, "end": v(166.69, 414.34) * mm, "construction": true});
            skLineSegment(sketch, "E109.0.4.40", {"start": v(190.5, 414.34) * mm, "end": v(190.5, 438.15) * mm, "construction": true});
            skLineSegment(sketch, "E109.0.4.41", {"start": v(128.59, 438.15) * mm, "end": v(128.59, 414.34) * mm, "construction": true});
            skCircle(sketch, "E109.0.5.0", {"center": v(66.67, 350.04) * mm, "radius": 11.11 * mm});
            skLineSegment(sketch, "E109.0.5.1", {"start": v(19.05, 350.04) * mm, "end": v(42.86, 350.04) * mm, "construction": true});
            skCircle(sketch, "E109.0.5.2", {"center": v(252.41, 338.14) * mm, "radius": 11.11 * mm});
            skLineSegment(sketch, "E109.0.5.3", {"start": v(104.78, 338.14) * mm, "end": v(128.59, 338.14) * mm, "construction": true});
            skLineSegment(sketch, "E109.0.5.4", {"start": v(19.05, 350.04) * mm, "end": v(0, 350.04) * mm, "construction": true});
            skCircle(sketch, "E109.0.5.5", {"center": v(228.6, 338.14) * mm, "radius": 11.11 * mm});
            skLineSegment(sketch, "E109.0.5.6", {"start": v(252.41, 338.14) * mm, "end": v(228.6, 338.14) * mm, "construction": true});
            skCircle(sketch, "E109.0.5.7", {"center": v(19.05, 350.04) * mm, "radius": 11.11 * mm});
            skCircle(sketch, "E109.0.5.8", {"center": v(128.59, 338.14) * mm, "radius": 11.11 * mm});
            skCircle(sketch, "E109.0.5.9", {"center": v(314.33, 350.04) * mm, "radius": 11.11 * mm});
            skCircle(sketch, "E109.0.5.10", {"center": v(338.14, 350.04) * mm, "radius": 11.11 * mm});
            skCircle(sketch, "E109.0.5.11", {"center": v(166.69, 338.14) * mm, "radius": 11.11 * mm});
            skCircle(sketch, "E109.0.5.12", {"center": v(190.5, 338.14) * mm, "radius": 11.11 * mm});
            skCircle(sketch, "E109.0.5.13", {"center": v(104.78, 338.14) * mm, "radius": 11.11 * mm});
            skCircle(sketch, "E109.0.5.14", {"center": v(42.86, 350.04) * mm, "radius": 11.11 * mm});
            skCircle(sketch, "E109.0.5.15", {"center": v(290.51, 350.04) * mm, "radius": 11.11 * mm});
            skLineSegment(sketch, "E109.0.5.16", {"start": v(290.51, 350.04) * mm, "end": v(314.33, 350.04) * mm, "construction": true});
            skCircle(sketch, "E109.0.5.17", {"center": v(128.59, 361.95) * mm, "radius": 11.11 * mm});
            skLineSegment(sketch, "E109.0.5.18", {"start": v(338.14, 350.04) * mm, "end": v(314.33, 350.04) * mm, "construction": true});
            skLineSegment(sketch, "E109.0.5.19", {"start": v(42.86, 350.04) * mm, "end": v(66.67, 350.04) * mm, "construction": true});
            skLineSegment(sketch, "E109.0.5.20", {"start": v(128.59, 361.95) * mm, "end": v(104.78, 361.95) * mm, "construction": true});
            skLineSegment(sketch, "E109.0.5.21", {"start": v(228.6, 350.04) * mm, "end": v(190.5, 350.04) * mm, "construction": true});
            skLineSegment(sketch, "E109.0.5.22", {"start": v(338.14, 350.04) * mm, "end": v(357.19, 350.04) * mm, "construction": true});
            skCircle(sketch, "E109.0.5.23", {"center": v(228.6, 361.95) * mm, "radius": 11.11 * mm});
            skCircle(sketch, "E109.0.5.24", {"center": v(104.78, 361.95) * mm, "radius": 11.11 * mm});
            skLineSegment(sketch, "E109.0.5.25", {"start": v(104.78, 350.04) * mm, "end": v(66.67, 350.04) * mm, "construction": true});
            skCircle(sketch, "E109.0.5.26", {"center": v(166.69, 361.95) * mm, "radius": 11.11 * mm});
            skCircle(sketch, "E109.0.5.27", {"center": v(252.41, 361.95) * mm, "radius": 11.11 * mm});
            skLineSegment(sketch, "E109.0.5.28", {"start": v(166.69, 361.95) * mm, "end": v(190.5, 361.95) * mm, "construction": true});
            skLineSegment(sketch, "E109.0.5.29", {"start": v(166.69, 338.14) * mm, "end": v(190.5, 338.14) * mm, "construction": true});
            skCircle(sketch, "E109.0.5.30", {"center": v(190.5, 361.95) * mm, "radius": 11.11 * mm});
            skLineSegment(sketch, "E109.0.5.31", {"start": v(252.41, 350.04) * mm, "end": v(290.51, 350.04) * mm, "construction": true});
            skLineSegment(sketch, "E109.0.5.32", {"start": v(252.41, 338.14) * mm, "end": v(252.41, 361.95) * mm, "construction": true});
            skLineSegment(sketch, "E109.0.5.33", {"start": v(104.78, 338.14) * mm, "end": v(104.78, 361.95) * mm, "construction": true});
            skLineSegment(sketch, "E109.0.5.34", {"start": v(155.58, 361.95) * mm, "end": v(155.58, 338.14) * mm, "construction": true});
            skLineSegment(sketch, "E109.0.5.35", {"start": v(228.6, 361.95) * mm, "end": v(252.41, 361.95) * mm, "construction": true});
            skLineSegment(sketch, "E109.0.5.36", {"start": v(139.7, 361.95) * mm, "end": v(139.7, 338.14) * mm, "construction": true});
            skLineSegment(sketch, "E109.0.5.37", {"start": v(128.59, 350.04) * mm, "end": v(166.69, 350.04) * mm, "construction": true});
            skLineSegment(sketch, "E109.0.5.38", {"start": v(228.6, 361.95) * mm, "end": v(228.6, 338.14) * mm, "construction": true});
            skLineSegment(sketch, "E109.0.5.39", {"start": v(166.69, 361.95) * mm, "end": v(166.69, 338.14) * mm, "construction": true});
            skLineSegment(sketch, "E109.0.5.40", {"start": v(190.5, 338.14) * mm, "end": v(190.5, 361.95) * mm, "construction": true});
            skLineSegment(sketch, "E109.0.5.41", {"start": v(128.59, 361.95) * mm, "end": v(128.59, 338.14) * mm, "construction": true});
            skCircle(sketch, "E109.0.6.0", {"center": v(66.67, 273.84) * mm, "radius": 11.11 * mm});
            skLineSegment(sketch, "E109.0.6.1", {"start": v(19.05, 273.84) * mm, "end": v(42.86, 273.84) * mm, "construction": true});
            skCircle(sketch, "E109.0.6.2", {"center": v(252.41, 261.94) * mm, "radius": 11.11 * mm});
            skLineSegment(sketch, "E109.0.6.3", {"start": v(104.78, 261.94) * mm, "end": v(128.59, 261.94) * mm, "construction": true});
            skLineSegment(sketch, "E109.0.6.4", {"start": v(19.05, 273.84) * mm, "end": v(0, 273.84) * mm, "construction": true});
            skCircle(sketch, "E109.0.6.5", {"center": v(228.6, 261.94) * mm, "radius": 11.11 * mm});
            skLineSegment(sketch, "E109.0.6.6", {"start": v(252.41, 261.94) * mm, "end": v(228.6, 261.94) * mm, "construction": true});
            skCircle(sketch, "E109.0.6.7", {"center": v(19.05, 273.84) * mm, "radius": 11.11 * mm});
            skCircle(sketch, "E109.0.6.8", {"center": v(128.59, 261.94) * mm, "radius": 11.11 * mm});
            skCircle(sketch, "E109.0.6.9", {"center": v(314.33, 273.84) * mm, "radius": 11.11 * mm});
            skCircle(sketch, "E109.0.6.10", {"center": v(338.14, 273.84) * mm, "radius": 11.11 * mm});
            skCircle(sketch, "E109.0.6.11", {"center": v(166.69, 261.94) * mm, "radius": 11.11 * mm});
            skCircle(sketch, "E109.0.6.12", {"center": v(190.5, 261.94) * mm, "radius": 11.11 * mm});
            skCircle(sketch, "E109.0.6.13", {"center": v(104.78, 261.94) * mm, "radius": 11.11 * mm});
            skCircle(sketch, "E109.0.6.14", {"center": v(42.86, 273.84) * mm, "radius": 11.11 * mm});
            skCircle(sketch, "E109.0.6.15", {"center": v(290.51, 273.84) * mm, "radius": 11.11 * mm});
            skLineSegment(sketch, "E109.0.6.16", {"start": v(290.51, 273.84) * mm, "end": v(314.33, 273.84) * mm, "construction": true});
            skCircle(sketch, "E109.0.6.17", {"center": v(128.59, 285.75) * mm, "radius": 11.11 * mm});
            skLineSegment(sketch, "E109.0.6.18", {"start": v(338.14, 273.84) * mm, "end": v(314.33, 273.84) * mm, "construction": true});
            skLineSegment(sketch, "E109.0.6.19", {"start": v(42.86, 273.84) * mm, "end": v(66.67, 273.84) * mm, "construction": true});
            skLineSegment(sketch, "E109.0.6.20", {"start": v(128.59, 285.75) * mm, "end": v(104.78, 285.75) * mm, "construction": true});
            skLineSegment(sketch, "E109.0.6.21", {"start": v(228.6, 273.84) * mm, "end": v(190.5, 273.84) * mm, "construction": true});
            skLineSegment(sketch, "E109.0.6.22", {"start": v(338.14, 273.84) * mm, "end": v(357.19, 273.84) * mm, "construction": true});
            skCircle(sketch, "E109.0.6.23", {"center": v(228.6, 285.75) * mm, "radius": 11.11 * mm});
            skCircle(sketch, "E109.0.6.24", {"center": v(104.78, 285.75) * mm, "radius": 11.11 * mm});
            skLineSegment(sketch, "E109.0.6.25", {"start": v(104.78, 273.84) * mm, "end": v(66.67, 273.84) * mm, "construction": true});
            skCircle(sketch, "E109.0.6.26", {"center": v(166.69, 285.75) * mm, "radius": 11.11 * mm});
            skCircle(sketch, "E109.0.6.27", {"center": v(252.41, 285.75) * mm, "radius": 11.11 * mm});
            skLineSegment(sketch, "E109.0.6.28", {"start": v(166.69, 285.75) * mm, "end": v(190.5, 285.75) * mm, "construction": true});
            skLineSegment(sketch, "E109.0.6.29", {"start": v(166.69, 261.94) * mm, "end": v(190.5, 261.94) * mm, "construction": true});
            skCircle(sketch, "E109.0.6.30", {"center": v(190.5, 285.75) * mm, "radius": 11.11 * mm});
            skLineSegment(sketch, "E109.0.6.31", {"start": v(252.41, 273.84) * mm, "end": v(290.51, 273.84) * mm, "construction": true});
            skLineSegment(sketch, "E109.0.6.32", {"start": v(252.41, 261.94) * mm, "end": v(252.41, 285.75) * mm, "construction": true});
            skLineSegment(sketch, "E109.0.6.33", {"start": v(104.78, 261.94) * mm, "end": v(104.78, 285.75) * mm, "construction": true});
            skLineSegment(sketch, "E109.0.6.34", {"start": v(155.58, 285.75) * mm, "end": v(155.58, 261.94) * mm, "construction": true});
            skLineSegment(sketch, "E109.0.6.35", {"start": v(228.6, 285.75) * mm, "end": v(252.41, 285.75) * mm, "construction": true});
            skLineSegment(sketch, "E109.0.6.36", {"start": v(139.7, 285.75) * mm, "end": v(139.7, 261.94) * mm, "construction": true});
            skLineSegment(sketch, "E109.0.6.37", {"start": v(128.59, 273.84) * mm, "end": v(166.69, 273.84) * mm, "construction": true});
            skLineSegment(sketch, "E109.0.6.38", {"start": v(228.6, 285.75) * mm, "end": v(228.6, 261.94) * mm, "construction": true});
            skLineSegment(sketch, "E109.0.6.39", {"start": v(166.69, 285.75) * mm, "end": v(166.69, 261.94) * mm, "construction": true});
            skLineSegment(sketch, "E109.0.6.40", {"start": v(190.5, 261.94) * mm, "end": v(190.5, 285.75) * mm, "construction": true});
            skLineSegment(sketch, "E109.0.6.41", {"start": v(128.59, 285.75) * mm, "end": v(128.59, 261.94) * mm, "construction": true});
            skCircle(sketch, "E109.0.7.0", {"center": v(66.67, 197.64) * mm, "radius": 11.11 * mm});
            skLineSegment(sketch, "E109.0.7.1", {"start": v(19.05, 197.64) * mm, "end": v(42.86, 197.64) * mm, "construction": true});
            skCircle(sketch, "E109.0.7.2", {"center": v(252.41, 185.74) * mm, "radius": 11.11 * mm});
            skLineSegment(sketch, "E109.0.7.3", {"start": v(104.78, 185.74) * mm, "end": v(128.59, 185.74) * mm, "construction": true});
            skLineSegment(sketch, "E109.0.7.4", {"start": v(19.05, 197.64) * mm, "end": v(0, 197.64) * mm, "construction": true});
            skCircle(sketch, "E109.0.7.5", {"center": v(228.6, 185.74) * mm, "radius": 11.11 * mm});
            skLineSegment(sketch, "E109.0.7.6", {"start": v(252.41, 185.74) * mm, "end": v(228.6, 185.74) * mm, "construction": true});
            skCircle(sketch, "E109.0.7.7", {"center": v(19.05, 197.64) * mm, "radius": 11.11 * mm});
            skCircle(sketch, "E109.0.7.8", {"center": v(128.59, 185.74) * mm, "radius": 11.11 * mm});
            skCircle(sketch, "E109.0.7.9", {"center": v(314.33, 197.64) * mm, "radius": 11.11 * mm});
            skCircle(sketch, "E109.0.7.10", {"center": v(338.14, 197.64) * mm, "radius": 11.11 * mm});
            skCircle(sketch, "E109.0.7.11", {"center": v(166.69, 185.74) * mm, "radius": 11.11 * mm});
            skCircle(sketch, "E109.0.7.12", {"center": v(190.5, 185.74) * mm, "radius": 11.11 * mm});
            skCircle(sketch, "E109.0.7.13", {"center": v(104.78, 185.74) * mm, "radius": 11.11 * mm});
            skCircle(sketch, "E109.0.7.14", {"center": v(42.86, 197.64) * mm, "radius": 11.11 * mm});
            skCircle(sketch, "E109.0.7.15", {"center": v(290.51, 197.64) * mm, "radius": 11.11 * mm});
            skLineSegment(sketch, "E109.0.7.16", {"start": v(290.51, 197.64) * mm, "end": v(314.33, 197.64) * mm, "construction": true});
            skCircle(sketch, "E109.0.7.17", {"center": v(128.59, 209.55) * mm, "radius": 11.11 * mm});
            skLineSegment(sketch, "E109.0.7.18", {"start": v(338.14, 197.64) * mm, "end": v(314.33, 197.64) * mm, "construction": true});
            skLineSegment(sketch, "E109.0.7.19", {"start": v(42.86, 197.64) * mm, "end": v(66.67, 197.64) * mm, "construction": true});
            skLineSegment(sketch, "E109.0.7.20", {"start": v(128.59, 209.55) * mm, "end": v(104.78, 209.55) * mm, "construction": true});
            skLineSegment(sketch, "E109.0.7.21", {"start": v(228.6, 197.64) * mm, "end": v(190.5, 197.64) * mm, "construction": true});
            skLineSegment(sketch, "E109.0.7.22", {"start": v(338.14, 197.64) * mm, "end": v(357.19, 197.64) * mm, "construction": true});
            skCircle(sketch, "E109.0.7.23", {"center": v(228.6, 209.55) * mm, "radius": 11.11 * mm});
            skCircle(sketch, "E109.0.7.24", {"center": v(104.78, 209.55) * mm, "radius": 11.11 * mm});
            skLineSegment(sketch, "E109.0.7.25", {"start": v(104.78, 197.64) * mm, "end": v(66.67, 197.64) * mm, "construction": true});
            skCircle(sketch, "E109.0.7.26", {"center": v(166.69, 209.55) * mm, "radius": 11.11 * mm});
            skCircle(sketch, "E109.0.7.27", {"center": v(252.41, 209.55) * mm, "radius": 11.11 * mm});
            skLineSegment(sketch, "E109.0.7.28", {"start": v(166.69, 209.55) * mm, "end": v(190.5, 209.55) * mm, "construction": true});
            skLineSegment(sketch, "E109.0.7.29", {"start": v(166.69, 185.74) * mm, "end": v(190.5, 185.74) * mm, "construction": true});
            skCircle(sketch, "E109.0.7.30", {"center": v(190.5, 209.55) * mm, "radius": 11.11 * mm});
            skLineSegment(sketch, "E109.0.7.31", {"start": v(252.41, 197.64) * mm, "end": v(290.51, 197.64) * mm, "construction": true});
            skLineSegment(sketch, "E109.0.7.32", {"start": v(252.41, 185.74) * mm, "end": v(252.41, 209.55) * mm, "construction": true});
            skLineSegment(sketch, "E109.0.7.33", {"start": v(104.78, 185.74) * mm, "end": v(104.78, 209.55) * mm, "construction": true});
            skLineSegment(sketch, "E109.0.7.34", {"start": v(155.57, 209.55) * mm, "end": v(155.57, 185.74) * mm, "construction": true});
            skLineSegment(sketch, "E109.0.7.35", {"start": v(228.6, 209.55) * mm, "end": v(252.41, 209.55) * mm, "construction": true});
            skLineSegment(sketch, "E109.0.7.36", {"start": v(139.7, 209.55) * mm, "end": v(139.7, 185.74) * mm, "construction": true});
            skLineSegment(sketch, "E109.0.7.37", {"start": v(128.59, 197.64) * mm, "end": v(166.69, 197.64) * mm, "construction": true});
            skLineSegment(sketch, "E109.0.7.38", {"start": v(228.6, 209.55) * mm, "end": v(228.6, 185.74) * mm, "construction": true});
            skLineSegment(sketch, "E109.0.7.39", {"start": v(166.69, 209.55) * mm, "end": v(166.69, 185.74) * mm, "construction": true});
            skLineSegment(sketch, "E109.0.7.40", {"start": v(190.5, 185.74) * mm, "end": v(190.5, 209.55) * mm, "construction": true});
            skLineSegment(sketch, "E109.0.7.41", {"start": v(128.59, 209.55) * mm, "end": v(128.59, 185.74) * mm, "construction": true});
            skLineSegment(sketch, "E109.direction1", {"start": v(0, 731.04) * mm, "end": v(25.4, 731.04) * mm, "construction": true});
            skLineSegment(sketch, "E109.direction2", {"start": v(0, 731.04) * mm, "end": v(0, 654.84) * mm, "construction": true});
            skCircle(sketch, "E110.0.0.8", {"center": v(66.67, 121.44) * mm, "radius": 11.11 * mm});
            skLineSegment(sketch, "E110.2.0.8", {"start": v(19.05, 121.44) * mm, "end": v(42.86, 121.44) * mm, "construction": true});
            skCircle(sketch, "E110.5.0.8", {"center": v(252.41, 109.54) * mm, "radius": 11.11 * mm});
            skLineSegment(sketch, "E110.7.0.8", {"start": v(104.78, 109.54) * mm, "end": v(128.59, 109.54) * mm, "construction": true});
            skLineSegment(sketch, "E110.10.0.8", {"start": v(19.05, 121.44) * mm, "end": v(0, 121.44) * mm, "construction": true});
            skCircle(sketch, "E110.13.0.8", {"center": v(228.6, 109.54) * mm, "radius": 11.11 * mm});
            skLineSegment(sketch, "E110.15.0.8", {"start": v(252.41, 109.54) * mm, "end": v(228.6, 109.54) * mm, "construction": true});
            skCircle(sketch, "E110.18.0.8", {"center": v(19.05, 121.44) * mm, "radius": 11.11 * mm});
            skCircle(sketch, "E110.20.0.8", {"center": v(128.59, 109.54) * mm, "radius": 11.11 * mm});
            skCircle(sketch, "E110.22.0.8", {"center": v(314.33, 121.44) * mm, "radius": 11.11 * mm});
            skCircle(sketch, "E110.24.0.8", {"center": v(338.14, 121.44) * mm, "radius": 11.11 * mm});
            skCircle(sketch, "E110.26.0.8", {"center": v(166.69, 109.54) * mm, "radius": 11.11 * mm});
            skCircle(sketch, "E110.28.0.8", {"center": v(190.5, 109.54) * mm, "radius": 11.11 * mm});
            skCircle(sketch, "E110.30.0.8", {"center": v(104.78, 109.54) * mm, "radius": 11.11 * mm});
            skCircle(sketch, "E110.32.0.8", {"center": v(42.86, 121.44) * mm, "radius": 11.11 * mm});
            skCircle(sketch, "E110.34.0.8", {"center": v(290.51, 121.44) * mm, "radius": 11.11 * mm});
            skLineSegment(sketch, "E110.36.0.8", {"start": v(290.51, 121.44) * mm, "end": v(314.33, 121.44) * mm, "construction": true});
            skCircle(sketch, "E110.39.0.8", {"center": v(128.59, 133.35) * mm, "radius": 11.11 * mm});
            skLineSegment(sketch, "E110.41.0.8", {"start": v(338.14, 121.44) * mm, "end": v(314.33, 121.44) * mm, "construction": true});
            skLineSegment(sketch, "E110.44.0.8", {"start": v(42.86, 121.44) * mm, "end": v(66.67, 121.44) * mm, "construction": true});
            skLineSegment(sketch, "E110.47.0.8", {"start": v(128.59, 133.35) * mm, "end": v(104.78, 133.35) * mm, "construction": true});
            skLineSegment(sketch, "E110.50.0.8", {"start": v(228.6, 121.44) * mm, "end": v(190.5, 121.44) * mm, "construction": true});
            skLineSegment(sketch, "E110.53.0.8", {"start": v(338.14, 121.44) * mm, "end": v(357.19, 121.44) * mm, "construction": true});
            skCircle(sketch, "E110.56.0.8", {"center": v(228.6, 133.35) * mm, "radius": 11.11 * mm});
            skCircle(sketch, "E110.58.0.8", {"center": v(104.78, 133.35) * mm, "radius": 11.11 * mm});
            skLineSegment(sketch, "E110.60.0.8", {"start": v(104.78, 121.44) * mm, "end": v(66.67, 121.44) * mm, "construction": true});
            skCircle(sketch, "E110.63.0.8", {"center": v(166.69, 133.35) * mm, "radius": 11.11 * mm});
            skCircle(sketch, "E110.65.0.8", {"center": v(252.41, 133.35) * mm, "radius": 11.11 * mm});
            skLineSegment(sketch, "E110.67.0.8", {"start": v(166.69, 133.35) * mm, "end": v(190.5, 133.35) * mm, "construction": true});
            skLineSegment(sketch, "E110.70.0.8", {"start": v(166.69, 109.54) * mm, "end": v(190.5, 109.54) * mm, "construction": true});
            skCircle(sketch, "E110.73.0.8", {"center": v(190.5, 133.35) * mm, "radius": 11.11 * mm});
            skLineSegment(sketch, "E110.75.0.8", {"start": v(252.41, 121.44) * mm, "end": v(290.51, 121.44) * mm, "construction": true});
            skLineSegment(sketch, "E110.78.0.8", {"start": v(252.41, 109.54) * mm, "end": v(252.41, 133.35) * mm, "construction": true});
            skLineSegment(sketch, "E110.81.0.8", {"start": v(104.77, 109.54) * mm, "end": v(104.77, 133.35) * mm, "construction": true});
            skLineSegment(sketch, "E110.84.0.8", {"start": v(155.57, 133.35) * mm, "end": v(155.57, 109.54) * mm, "construction": true});
            skLineSegment(sketch, "E110.87.0.8", {"start": v(228.6, 133.35) * mm, "end": v(252.41, 133.35) * mm, "construction": true});
            skLineSegment(sketch, "E110.90.0.8", {"start": v(139.7, 133.35) * mm, "end": v(139.7, 109.54) * mm, "construction": true});
            skLineSegment(sketch, "E110.93.0.8", {"start": v(128.59, 121.44) * mm, "end": v(166.69, 121.44) * mm, "construction": true});
            skLineSegment(sketch, "E110.96.0.8", {"start": v(228.6, 133.35) * mm, "end": v(228.6, 109.54) * mm, "construction": true});
            skLineSegment(sketch, "E110.99.0.8", {"start": v(166.69, 133.35) * mm, "end": v(166.69, 109.54) * mm, "construction": true});
            skLineSegment(sketch, "E110.102.0.8", {"start": v(190.5, 109.54) * mm, "end": v(190.5, 133.35) * mm, "construction": true});
            skLineSegment(sketch, "E110.105.0.8", {"start": v(128.59, 133.35) * mm, "end": v(128.59, 109.54) * mm, "construction": true});
            skCircle(sketch, "E110.0.0.9", {"center": v(66.67, 45.24) * mm, "radius": 11.11 * mm});
            skLineSegment(sketch, "E110.2.0.9", {"start": v(19.05, 45.24) * mm, "end": v(42.86, 45.24) * mm, "construction": true});
            skCircle(sketch, "E110.5.0.9", {"center": v(252.41, 33.34) * mm, "radius": 11.11 * mm});
            skLineSegment(sketch, "E110.7.0.9", {"start": v(104.78, 33.34) * mm, "end": v(128.59, 33.34) * mm, "construction": true});
            skLineSegment(sketch, "E110.10.0.9", {"start": v(19.05, 45.24) * mm, "end": v(0, 45.24) * mm, "construction": true});
            skCircle(sketch, "E110.13.0.9", {"center": v(228.6, 33.34) * mm, "radius": 11.11 * mm});
            skLineSegment(sketch, "E110.15.0.9", {"start": v(252.41, 33.34) * mm, "end": v(228.6, 33.34) * mm, "construction": true});
            skCircle(sketch, "E110.18.0.9", {"center": v(19.05, 45.24) * mm, "radius": 11.11 * mm});
            skCircle(sketch, "E110.20.0.9", {"center": v(128.59, 33.34) * mm, "radius": 11.11 * mm});
            skCircle(sketch, "E110.22.0.9", {"center": v(314.33, 45.24) * mm, "radius": 11.11 * mm});
            skCircle(sketch, "E110.24.0.9", {"center": v(338.14, 45.24) * mm, "radius": 11.11 * mm});
            skCircle(sketch, "E110.26.0.9", {"center": v(166.69, 33.34) * mm, "radius": 11.11 * mm});
            skCircle(sketch, "E110.28.0.9", {"center": v(190.5, 33.34) * mm, "radius": 11.11 * mm});
            skCircle(sketch, "E110.30.0.9", {"center": v(104.78, 33.34) * mm, "radius": 11.11 * mm});
            skCircle(sketch, "E110.32.0.9", {"center": v(42.86, 45.24) * mm, "radius": 11.11 * mm});
            skCircle(sketch, "E110.34.0.9", {"center": v(290.51, 45.24) * mm, "radius": 11.11 * mm});
            skLineSegment(sketch, "E110.36.0.9", {"start": v(290.51, 45.24) * mm, "end": v(314.33, 45.24) * mm, "construction": true});
            skCircle(sketch, "E110.39.0.9", {"center": v(128.59, 57.15) * mm, "radius": 11.11 * mm});
            skLineSegment(sketch, "E110.41.0.9", {"start": v(338.14, 45.24) * mm, "end": v(314.33, 45.24) * mm, "construction": true});
            skLineSegment(sketch, "E110.44.0.9", {"start": v(42.86, 45.24) * mm, "end": v(66.67, 45.24) * mm, "construction": true});
            skLineSegment(sketch, "E110.47.0.9", {"start": v(128.59, 57.15) * mm, "end": v(104.78, 57.15) * mm, "construction": true});
            skLineSegment(sketch, "E110.50.0.9", {"start": v(228.6, 45.24) * mm, "end": v(190.5, 45.24) * mm, "construction": true});
            skLineSegment(sketch, "E110.53.0.9", {"start": v(338.14, 45.24) * mm, "end": v(357.19, 45.24) * mm, "construction": true});
            skCircle(sketch, "E110.56.0.9", {"center": v(228.6, 57.15) * mm, "radius": 11.11 * mm});
            skCircle(sketch, "E110.58.0.9", {"center": v(104.78, 57.15) * mm, "radius": 11.11 * mm});
            skLineSegment(sketch, "E110.60.0.9", {"start": v(104.78, 45.24) * mm, "end": v(66.67, 45.24) * mm, "construction": true});
            skCircle(sketch, "E110.63.0.9", {"center": v(166.69, 57.15) * mm, "radius": 11.11 * mm});
            skCircle(sketch, "E110.65.0.9", {"center": v(252.41, 57.15) * mm, "radius": 11.11 * mm});
            skLineSegment(sketch, "E110.67.0.9", {"start": v(166.69, 57.15) * mm, "end": v(190.5, 57.15) * mm, "construction": true});
            skLineSegment(sketch, "E110.70.0.9", {"start": v(166.69, 33.34) * mm, "end": v(190.5, 33.34) * mm, "construction": true});
            skCircle(sketch, "E110.73.0.9", {"center": v(190.5, 57.15) * mm, "radius": 11.11 * mm});
            skLineSegment(sketch, "E110.75.0.9", {"start": v(252.41, 45.24) * mm, "end": v(290.51, 45.24) * mm, "construction": true});
            skLineSegment(sketch, "E110.78.0.9", {"start": v(252.41, 33.34) * mm, "end": v(252.41, 57.15) * mm, "construction": true});
            skLineSegment(sketch, "E110.81.0.9", {"start": v(104.77, 33.34) * mm, "end": v(104.77, 57.15) * mm, "construction": true});
            skLineSegment(sketch, "E110.84.0.9", {"start": v(155.57, 57.15) * mm, "end": v(155.57, 33.34) * mm, "construction": true});
            skLineSegment(sketch, "E110.87.0.9", {"start": v(228.6, 57.15) * mm, "end": v(252.41, 57.15) * mm, "construction": true});
            skLineSegment(sketch, "E110.90.0.9", {"start": v(139.7, 57.15) * mm, "end": v(139.7, 33.34) * mm, "construction": true});
            skLineSegment(sketch, "E110.93.0.9", {"start": v(128.59, 45.24) * mm, "end": v(166.69, 45.24) * mm, "construction": true});
            skLineSegment(sketch, "E110.96.0.9", {"start": v(228.6, 57.15) * mm, "end": v(228.6, 33.34) * mm, "construction": true});
            skLineSegment(sketch, "E110.99.0.9", {"start": v(166.69, 57.15) * mm, "end": v(166.69, 33.34) * mm, "construction": true});
            skLineSegment(sketch, "E110.102.0.9", {"start": v(190.5, 33.34) * mm, "end": v(190.5, 57.15) * mm, "construction": true});
            skLineSegment(sketch, "E110.105.0.9", {"start": v(128.59, 57.15) * mm, "end": v(128.59, 33.34) * mm, "construction": true});
            skSolve(sketch);
        }
        {
            var Q0;
            Q0=makeQuery(id+"F1.imprint","IMPRINT",FACE,{"disambiguationData":[TD([[makeQuery(id+"F1.imprint","IMPRINT",EDGE,{"derivedFrom":sQuery(id+"F1.wireOp",EDGE,"E62")}),-1.0]])]});
            extrude(context, id + "F2", {"entities" : qUnion([Q0]), "depth" : 25.4 * mm});
        }
    });
